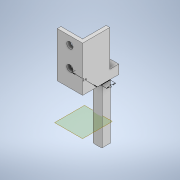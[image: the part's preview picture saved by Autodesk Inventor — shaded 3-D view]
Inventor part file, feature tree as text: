
AUTODESK INVENTOR PART (.ipt)
format: ipt  version: 2020 (Build 240168000, 168)  size: 308,736 bytes
history: native  units: mm
features: sketch x8, extrude x7, plane x1, fillet x1, projected_geometry x1
ambient origin geometry x8: Origin, YZ Plane, XZ Plane, XY Plane, X Axis, Y Axis, Z Axis, Center Point
bodies: Solid1 (feature_tree)
feature tree (18):
  extrude  "Extrusion1"  Depth=2.0mm
  extrude  "Extrusion2"  Depth=14.0mm
  extrude  "Extrusion3"  Depth=2.0mm
  sketch  "Sketch4"  dims[d6=20.0mm d7=0.0mm d8=4.5mm]
  plane  "Work Plane1"
  extrude  "Extrusion4"  Depth=4.5mm
  extrude  "Extrusion5"  Depth=11.0mm
  fillet  "Fillet1"  Radius=3.5mm
  extrude  "Extrusion7"  Depth=5.0mm TaperAngle=0.0deg
  extrude  "Extrusion8"  Depth=5.0mm
  sketch  "Sketch1"  dims[d0=13.0mm d1=2.0mm]
  sketch  "Sketch2"  dims[d2=15.0mm d3=14.0mm]
  sketch  "Sketch3"  dims[d4=2.0mm d5=13.0mm]
  sketch  "Sketch5"  dims[d9=3.5mm d10=11.0mm d11=3.5mm]
  sketch  "Sketch6"  dims[d12=20.0mm d13=0.0mm d14=5.0mm d15=0.0mm]
  sketch  "Sketch9"  dims[d16=14.0mm d17=5.0mm]
  projected_geometry  "Projected Loop1"
  sketch  "Sketch10"  dims[d18=20.0mm d20=20.0mm d21=0.0mm d25=2.5mm d26=5.0mm d27=5.0mm d28=20.0mm d29=0.0mm d31=12.5mm d32=2.0mm d35=15.0mm d36=0.0mm d37=10.0mm d38=0.0mm]
